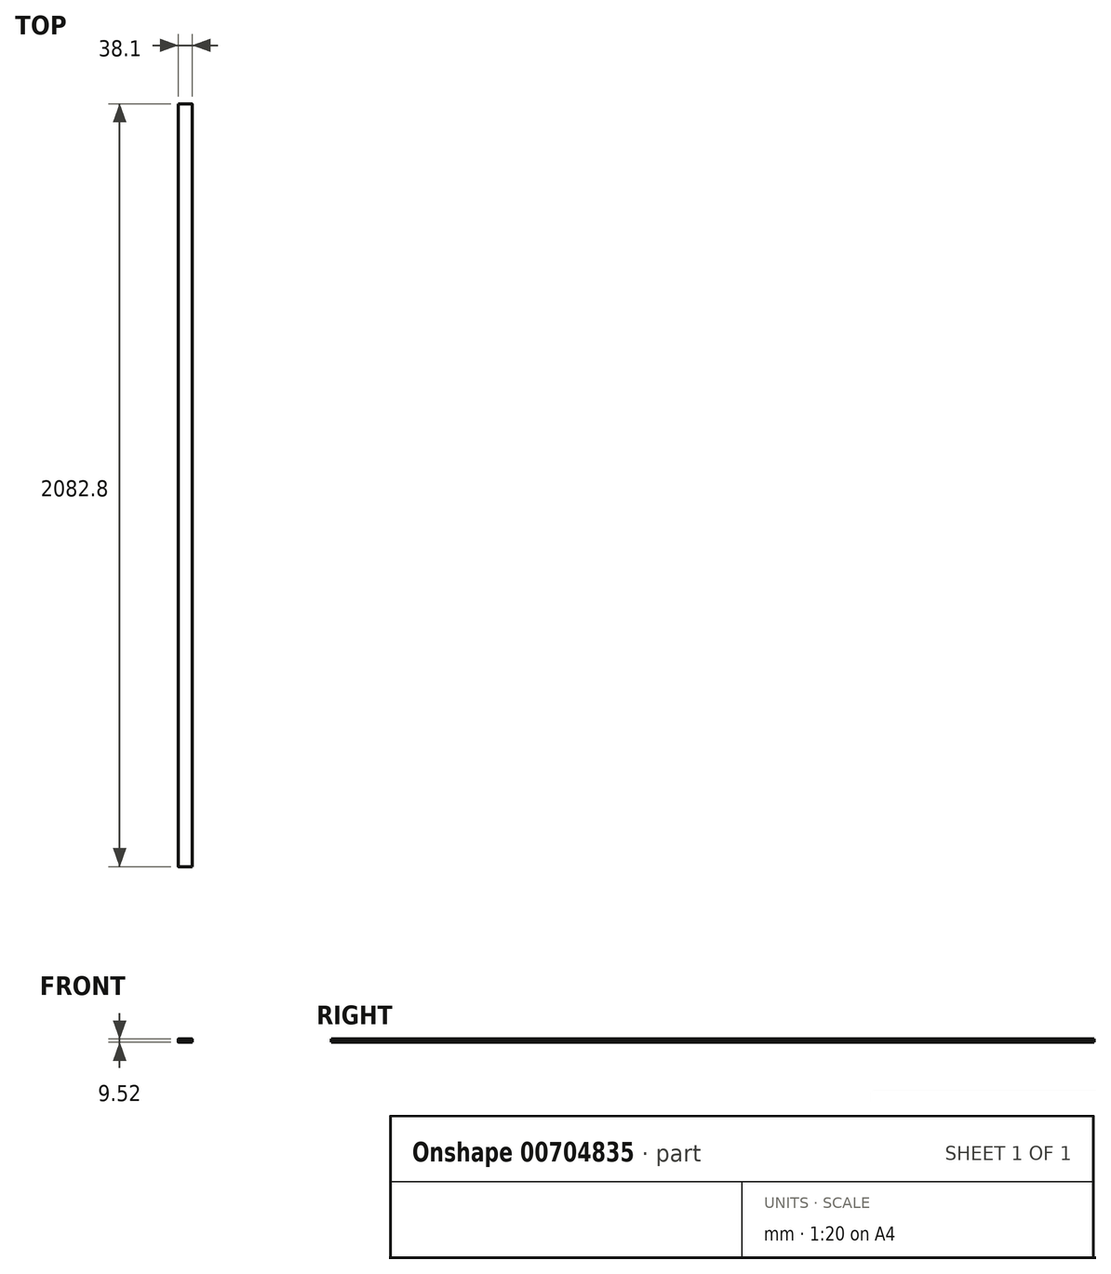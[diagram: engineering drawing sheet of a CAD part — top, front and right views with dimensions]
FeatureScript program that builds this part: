
annotation { "Feature Type Name" : "Feature", "Feature Type Description" : "" }
export const myFeature = defineFeature(function(context is Context, id is Id, definition is map)
    precondition{}
    {
        {
            var Q0;
            Q0=qCreatedBy(makeId("Front.planeOp"),FACE);
            var sketch = newSketch(context, id + "F0", { "sketchPlane" : qUnion([Q0])});
            skLineSegment(sketch, "E0.bottom", {"start": v(-46.07, 62.47) * mm, "end": v(-9.55, 62.47) * mm});
            skLineSegment(sketch, "E0.top", {"start": v(-46.07, 52.95) * mm, "end": v(-9.55, 52.95) * mm});
            skLineSegment(sketch, "E0.left", {"start": v(-46.86, 61.69) * mm, "end": v(-46.86, 53.74) * mm});
            skLineSegment(sketch, "E0.right", {"start": v(-8.76, 61.69) * mm, "end": v(-8.76, 53.74) * mm});
            skPoint(sketch, "E1.visualSharp", {"position": v(-46.86, 62.47) * mm});
            skArc(sketch, "E1.filletArc", {"start": v(-46.07, 62.47) * mm, "mid": v(-46.63, 62.24) * mm, "end": v(-46.86, 61.69) * mm});
            skPoint(sketch, "E2.visualSharp", {"position": v(-46.86, 52.95) * mm});
            skArc(sketch, "E2.filletArc", {"start": v(-46.86, 53.74) * mm, "mid": v(-46.63, 53.18) * mm, "end": v(-46.07, 52.95) * mm});
            skPoint(sketch, "E3.visualSharp", {"position": v(-8.76, 62.47) * mm});
            skArc(sketch, "E3.filletArc", {"start": v(-8.76, 61.69) * mm, "mid": v(-8.99, 62.24) * mm, "end": v(-9.55, 62.47) * mm});
            skPoint(sketch, "E4.visualSharp", {"position": v(-8.76, 52.95) * mm});
            skArc(sketch, "E4.filletArc", {"start": v(-9.55, 52.95) * mm, "mid": v(-8.99, 53.18) * mm, "end": v(-8.76, 53.74) * mm});
            skSolve(sketch);
        }
        {
            var Q0;
            Q0=makeQuery(id+"F0.imprint","IMPRINT",FACE,{"disambiguationData":[TD([[makeQuery(id+"F0.imprint","IMPRINT",EDGE,{"derivedFrom":sQuery(id+"F0.wireOp",EDGE,"E0.bottom")}),-1.0]])]});
            extrude(context, id + "F1", {"entities" : qUnion([Q0]), "depth" : 2082.8 * mm, "offsetDistance" : 25.4 * mm});
        }
    });
